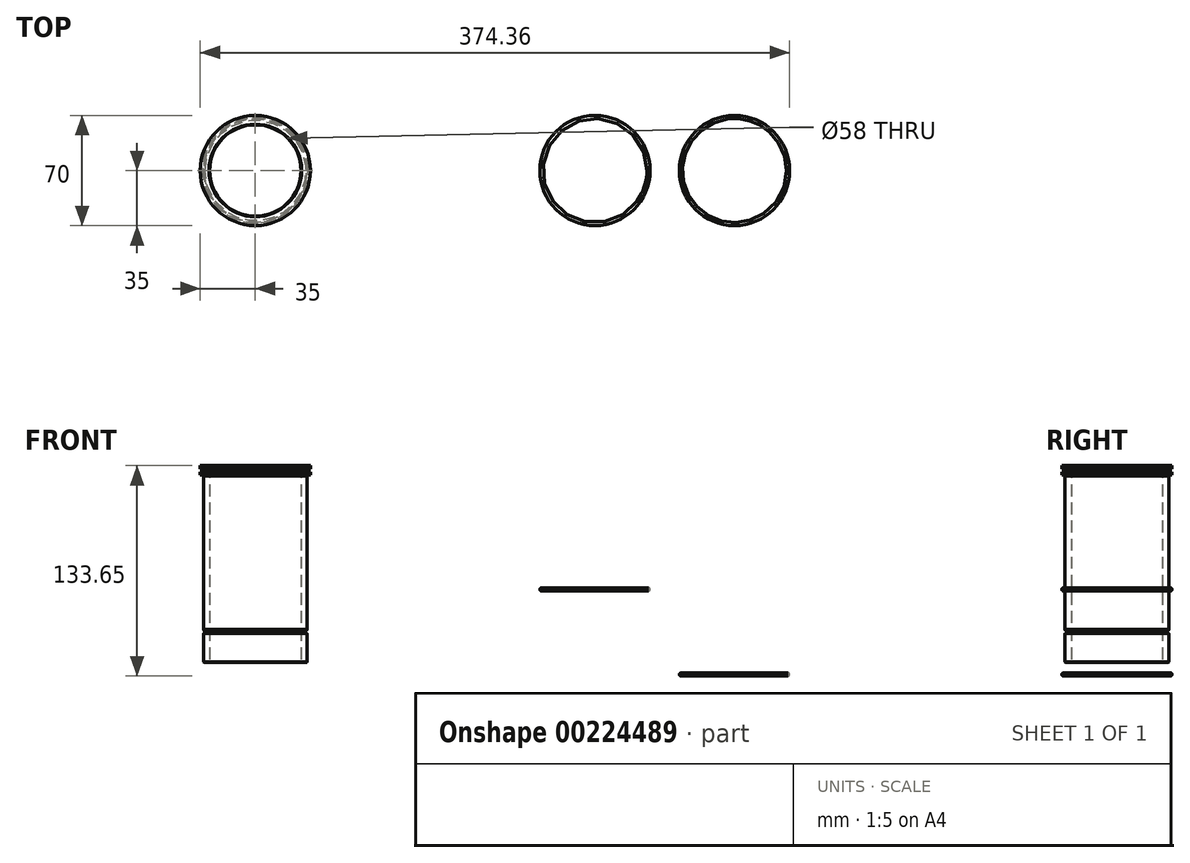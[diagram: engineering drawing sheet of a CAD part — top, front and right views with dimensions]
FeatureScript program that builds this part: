
annotation { "Feature Type Name" : "Feature", "Feature Type Description" : "" }
export const myFeature = defineFeature(function(context is Context, id is Id, definition is map)
    precondition{}
    {
        {
            var Q0;
            Q0=qCreatedBy(makeId("Front.planeOp"),FACE);
            var sketch = newSketch(context, id + "F0", { "sketchPlane" : qUnion([Q0])});
            skLineSegment(sketch, "E0", {"start": v(-159.67, 0) * mm, "end": v(159.27, 0) * mm, "construction": true});
            skLineSegment(sketch, "E1", {"start": v(-35, 125) * mm, "end": v(-29, 125) * mm});
            skLineSegment(sketch, "E2", {"start": v(-35, 125) * mm, "end": v(-35, 123) * mm});
            skLineSegment(sketch, "E3", {"start": v(-35, 123) * mm, "end": v(-33, 123) * mm});
            skLineSegment(sketch, "E4", {"start": v(-33, 123) * mm, "end": v(-33, 121) * mm});
            skLineSegment(sketch, "E5", {"start": v(-33, 121) * mm, "end": v(-35, 121) * mm});
            skLineSegment(sketch, "E6", {"start": v(-35, 121) * mm, "end": v(-35, 119) * mm});
            skLineSegment(sketch, "E7", {"start": v(-35, 119) * mm, "end": v(-33, 119) * mm});
            skLineSegment(sketch, "E8", {"start": v(-33, 119) * mm, "end": v(-33, 20.52) * mm});
            skLineSegment(sketch, "E9", {"start": v(-29, 125) * mm, "end": v(-29, 0) * mm});
            skLineSegment(sketch, "E10", {"start": v(0, 0) * mm, "end": v(0, 141.29) * mm, "construction": true});
            skLineSegment(sketch, "E11", {"start": v(-33, 0) * mm, "end": v(-29, 0) * mm});
            skPoint(sketch, "E12", {"position": v(-33, 20.52) * mm});
            skPoint(sketch, "E13", {"position": v(-33, 18.52) * mm});
            skArc(sketch, "E14", {"start": v(-33, 18.52) * mm, "mid": v(-32.04, 19.52) * mm, "end": v(-33, 20.52) * mm});
            skLineSegment(sketch, "E15.trimOffspring", {"start": v(-33, 18.52) * mm, "end": v(-33, 0) * mm});
            skSolve(sketch);
        }
        {
            var Q0;
            Q0=makeQuery(id+"F0.imprint","IMPRINT",FACE,{"disambiguationData":[TD([[makeQuery(id+"F0.imprint","IMPRINT",EDGE,{"derivedFrom":sQuery(id+"F0.wireOp",EDGE,"E1")}),-1.0]])]});
            var Q1;
            Q1=sQuery(id+"F0.wireOp",EDGE,"E10");
            revolve(context, id + "F1", {"entities" : qUnion([Q0]), "axis" : qUnion([Q1]), "revolveType" : RevolveType.FULL});
        }
        {
            var Q0;
            Q0=makeQuery(id+"F1.opRevolve","SWEPT_EDGE",EDGE,{"disambiguationData":[OSD([sQuery(id+"F0.wireOp",EDGE,"E8"),sQuery(id+"F0.wireOp",EDGE,"E11")])]});
            var Q1;
            Q1=makeQuery(id+"F1.opRevolve","SWEPT_EDGE",EDGE,{"disambiguationData":[OSD([sQuery(id+"F0.wireOp",EDGE,"E1"),sQuery(id+"F0.wireOp",EDGE,"E9")])]});
            var Q2;
            Q2=makeQuery(id+"F1.opRevolve","SWEPT_EDGE",EDGE,{"disambiguationData":[OSD([sQuery(id+"F0.wireOp",EDGE,"E9"),sQuery(id+"F0.wireOp",EDGE,"E11")])]});
            chamfer(context, id + "F2", {"entities" : qUnion([Q0, Q1, Q2]), "width" : .4 * mm, "tangentPropagation" : true});
        }
        {
            var Q0;
            Q0=qCreatedBy(makeId("Front.planeOp"),FACE);
            var sketch = newSketch(context, id + "F3", { "sketchPlane" : qUnion([Q0])});
            skLineSegment(sketch, "E16", {"start": v(304.36, 13.5) * mm, "end": v(304.36, -10.3) * mm, "construction": true});
            skLineSegment(sketch, "E17", {"start": v(304.36, -10.3) * mm, "end": v(283.13, -10.3) * mm, "construction": true});
            skCircle(sketch, "E18", {"center": v(270.36, -7.65) * mm, "radius": 1 * mm});
            skLineSegment(sketch, "E19", {"start": v(216.37, 70.35) * mm, "end": v(216.37, 46.56) * mm, "construction": true});
            skLineSegment(sketch, "E20", {"start": v(216.37, 46.56) * mm, "end": v(195.15, 46.56) * mm, "construction": true});
            skCircle(sketch, "E21", {"center": v(185.37, 49.22) * mm, "radius": 1 * mm});
            skSolve(sketch);
        }
        {
            var Q0;
            Q0 = qSketchRegion(id + "F3", true);
            var Q1;
            Q1=sQuery(id+"F3.wireOp",EDGE,"E16");
            revolve(context, id + "F4", {"entities" : qUnion([Q0]), "axis" : qUnion([Q1]), "revolveType" : RevolveType.FULL});
        }
        {
            var Q0;
            Q0=makeQuery(id+"F4.opRevolve","SWEPT_BODY",BODY,{"disambiguationData":[OSD([sQuery(id+"F3.wireOp",EDGE,"E21")])]});
            deleteBodies(context, id + "F5", {"entities" : qUnion([Q0])});
        }
        {
            var Q0;
            Q0=qCreatedBy(makeId("Front.planeOp"),FACE);
            var sketch = newSketch(context, id + "F6", { "sketchPlane" : qUnion([Q0])});
            skLineSegment(sketch, "E22", {"start": v(215.71, 102.72) * mm, "end": v(215.71, 35.45) * mm, "construction": true});
            skLineSegment(sketch, "E23", {"start": v(215.71, 35.45) * mm, "end": v(126.09, 35.45) * mm, "construction": true});
            skCircle(sketch, "E24", {"center": v(181.71, 46.44) * mm, "radius": 1 * mm});
            skSolve(sketch);
        }
        {
            var Q0;
            Q0=makeQuery(id+"F6.imprint","IMPRINT",FACE,{"disambiguationData":[TD([[makeQuery(id+"F6.imprint","IMPRINT",EDGE,{"derivedFrom":sQuery(id+"F6.wireOp",EDGE,"E24")}),1.0]])]});
            var Q1;
            Q1=sQuery(id+"F6.wireOp",EDGE,"E22");
            revolve(context, id + "F7", {"entities" : qUnion([Q0]), "axis" : qUnion([Q1]), "revolveType" : RevolveType.FULL});
        }
    });
